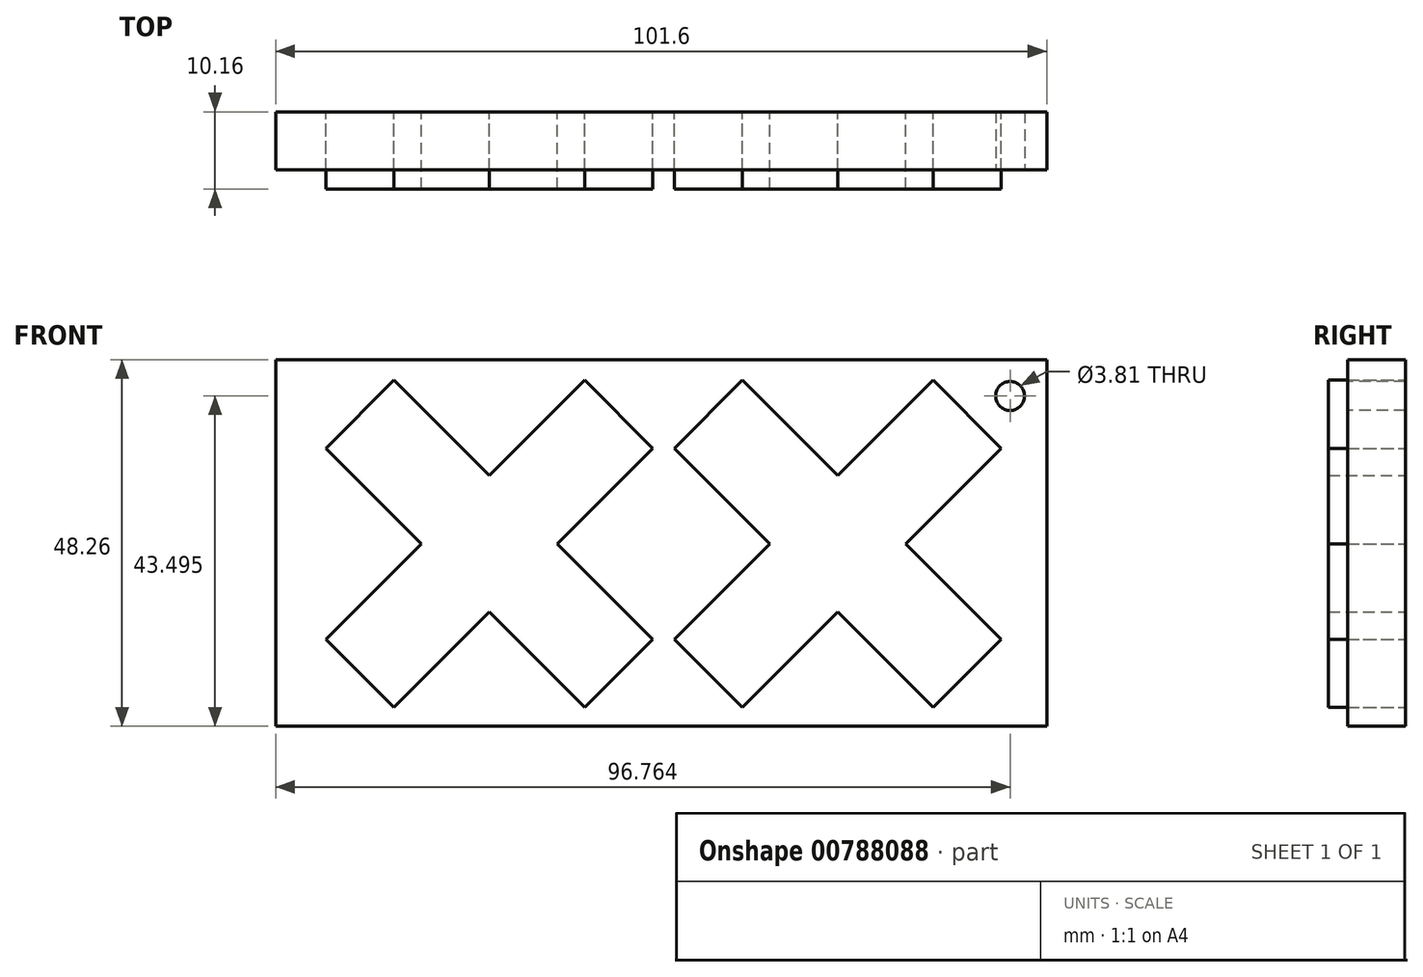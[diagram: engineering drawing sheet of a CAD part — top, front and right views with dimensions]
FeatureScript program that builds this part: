
annotation { "Feature Type Name" : "Feature", "Feature Type Description" : "" }
export const myFeature = defineFeature(function(context is Context, id is Id, definition is map)
    precondition{}
    {
        {
            var Q0;
            Q0=qCreatedBy(makeId("Front.planeOp"),FACE);
            var sketch = newSketch(context, id + "F0", { "sketchPlane" : qUnion([Q0])});
            skLineSegment(sketch, "E0", {"start": v(-52.49, 0) * mm, "end": v(-65.06, 12.57) * mm});
            skLineSegment(sketch, "E1", {"start": v(-65.06, 12.57) * mm, "end": v(-56.08, 21.55) * mm});
            skLineSegment(sketch, "E2", {"start": v(-56.08, 21.55) * mm, "end": v(-43.5, 8.98) * mm});
            skLineSegment(sketch, "E3", {"start": v(-43.5, 8.98) * mm, "end": v(-30.94, 21.55) * mm});
            skLineSegment(sketch, "E4", {"start": v(-30.94, 21.55) * mm, "end": v(-21.96, 12.57) * mm});
            skLineSegment(sketch, "E5", {"start": v(-21.96, 12.57) * mm, "end": v(-34.53, 0) * mm});
            skLineSegment(sketch, "E6", {"start": v(-34.53, 0) * mm, "end": v(-21.96, -12.57) * mm});
            skLineSegment(sketch, "E7", {"start": v(-21.96, -12.57) * mm, "end": v(-30.94, -21.55) * mm});
            skLineSegment(sketch, "E8", {"start": v(-30.94, -21.55) * mm, "end": v(-43.5, -8.98) * mm});
            skLineSegment(sketch, "E9", {"start": v(-43.5, -8.98) * mm, "end": v(-56.08, -21.55) * mm});
            skLineSegment(sketch, "E10", {"start": v(-56.08, -21.55) * mm, "end": v(-65.06, -12.57) * mm});
            skLineSegment(sketch, "E11", {"start": v(-65.06, -12.57) * mm, "end": v(-52.49, 0) * mm});
            skSolve(sketch);
        }
        {
            var Q0;
            Q0=makeQuery(id+"F0.imprint","IMPRINT",FACE,{"disambiguationData":[TD([[makeQuery(id+"F0.imprint","IMPRINT",EDGE,{"derivedFrom":sQuery(id+"F0.wireOp",EDGE,"E0")}),-1.0]])]});
            extrude(context, id + "F1", {"entities" : qUnion([Q0]), "depth" : 10.16 * mm, "offsetDistance" : 25.4 * mm});
        }
        {
            var Q0;
            Q0=qCreatedBy(makeId("Front.planeOp"),FACE);
            var sketch = newSketch(context, id + "F2", { "sketchPlane" : qUnion([Q0])});
            skLineSegment(sketch, "E12", {"start": v(-6.58, 0) * mm, "end": v(-19.15, 12.57) * mm});
            skLineSegment(sketch, "E13", {"start": v(-19.15, 12.57) * mm, "end": v(-10.17, 21.55) * mm});
            skLineSegment(sketch, "E14", {"start": v(-10.17, 21.55) * mm, "end": v(2.4, 8.98) * mm});
            skLineSegment(sketch, "E15", {"start": v(2.4, 8.98) * mm, "end": v(14.97, 21.55) * mm});
            skLineSegment(sketch, "E16", {"start": v(14.97, 21.55) * mm, "end": v(23.95, 12.57) * mm});
            skLineSegment(sketch, "E17", {"start": v(23.95, 12.57) * mm, "end": v(11.38, 0) * mm});
            skLineSegment(sketch, "E18", {"start": v(11.38, 0) * mm, "end": v(23.95, -12.57) * mm});
            skLineSegment(sketch, "E19", {"start": v(23.95, -12.57) * mm, "end": v(14.97, -21.55) * mm});
            skLineSegment(sketch, "E20", {"start": v(14.97, -21.55) * mm, "end": v(2.4, -8.98) * mm});
            skLineSegment(sketch, "E21", {"start": v(2.4, -8.98) * mm, "end": v(-10.17, -21.55) * mm});
            skLineSegment(sketch, "E22", {"start": v(-10.17, -21.55) * mm, "end": v(-19.15, -12.57) * mm});
            skLineSegment(sketch, "E23", {"start": v(-19.15, -12.57) * mm, "end": v(-6.58, 0) * mm});
            skSolve(sketch);
        }
        {
            var Q0;
            Q0=qCreatedBy(makeId("Front.planeOp"),FACE);
            var sketch = newSketch(context, id + "F3", { "sketchPlane" : qUnion([Q0])});
            skLineSegment(sketch, "E24.bottom", {"start": v(-71.66, 24.23) * mm, "end": v(29.94, 24.23) * mm});
            skLineSegment(sketch, "E24.top", {"start": v(-71.66, -24.03) * mm, "end": v(29.94, -24.03) * mm});
            skLineSegment(sketch, "E24.left", {"start": v(-71.66, 24.23) * mm, "end": v(-71.66, -24.03) * mm});
            skLineSegment(sketch, "E24.right", {"start": v(29.94, 24.23) * mm, "end": v(29.94, -24.03) * mm});
            skSolve(sketch);
        }
        {
            var Q0;
            Q0 = qSketchRegion(id + "F3", true);
            extrude(context, id + "F4", {"entities" : qUnion([Q0]), "depth" : 7.62 * mm, "offsetDistance" : 25.4 * mm});
        }
        {
            var Q0;
            Q0=makeQuery(id+"F4.opExtrude","CAP_FACE",FACE,{"disambiguationData":[OSD([sQuery(id+"F3.wireOp",EDGE,"E24.bottom"),sQuery(id+"F3.wireOp",EDGE,"E24.top"),sQuery(id+"F3.wireOp",EDGE,"E24.left"),sQuery(id+"F3.wireOp",EDGE,"E24.right")])],"isStart":false});
            var sketch = newSketch(context, id + "F5", { "sketchPlane" : qUnion([Q0])});
            skCircle(sketch, "E25", {"center": v(25.1, 19.47) * mm, "radius": 1.9 * mm});
            skText(sketch, "E26", { "text": "JH", "fontName": "OpenSans-Bold.ttf"});
            const initialGuessF5  = {"E26": [0.0184, -0.02403, 1, 0, 0.00725]};
            skSetInitialGuess(sketch, initialGuessF5);
            skSolve(sketch);
        }
        {
            var Q0;
            Q0=sQuery(id+"F5.wireOp",VERTEX,"E25.center");
            var Q1;
            Q1=makeQuery(id+"F4.opExtrude","SWEPT_BODY",BODY,{"disambiguationData":[OSD([sQuery(id+"F3.wireOp",EDGE,"E24.bottom"),sQuery(id+"F3.wireOp",EDGE,"E24.top"),sQuery(id+"F3.wireOp",EDGE,"E24.left"),sQuery(id+"F3.wireOp",EDGE,"E24.right")])]});
            hole(context, id + "F6", {"style" : HoleStyle.SIMPLE, "endStyle" : HoleEndStyle.THROUGH, "holeDiameter" : 3.8 * mm, "majorDiameter" : 6.35 * mm, "isTappedThrough" : true, "tappedDepth" : 12.7 * mm, "tapClearance" : 3, "locations" : qUnion([Q0]), "scope" : qUnion([Q1])});
        }
        {
            var Q0;
            Q0 = qSketchRegion(id + "F2", true);
            extrude(context, id + "F7", {"entities" : qUnion([Q0]), "depth" : 10.16 * mm, "offsetDistance" : 25.4 * mm});
        }
    });
